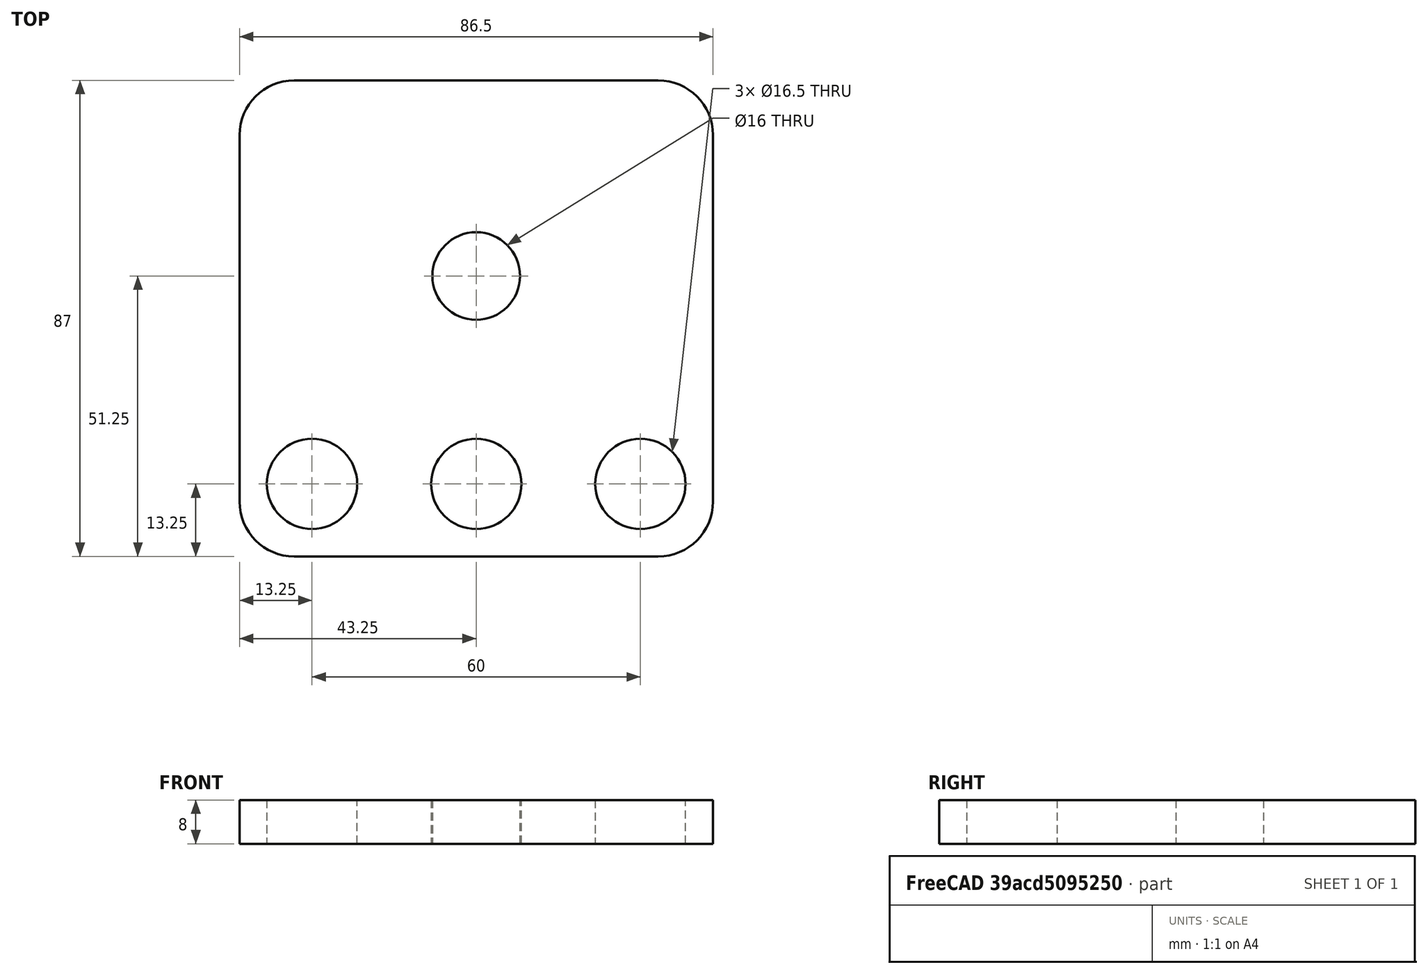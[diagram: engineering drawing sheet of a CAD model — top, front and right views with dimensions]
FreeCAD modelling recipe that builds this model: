
FCSTD DOCUMENT  (FreeCAD 0.19R24267 +99 (Git))
Label: V2 Allignment plate tabbed end plate
License: All rights reserved
LicenseURL: http://en.wikipedia.org/wiki/All_rights_reserved
objects: Sketcher::SketchObject×1, PartDesign::Pad×1, PartDesign::Body×1
note: 4 computed .brp shape members not serialized (recipe doc carries the construction recipe); baked Part::Feature solids carry a one-line shape summary decoded from their .brp

FEATURE [Sketcher::SketchObject] Sketch
  FullyConstrained = true
  MapMode = 5
  Support = -> [XY_Plane]
  sketch-geometry (17):
    g0: Circle CenterX=0 CenterY=0 CenterZ=0 NormalX=0 NormalY=0 NormalZ=1 AngleXU=0 Radius=6
    g1: Circle CenterX=0 CenterY=0 CenterZ=0 NormalX=0 NormalY=0 NormalZ=1 AngleXU=0 Radius=8
    g2: Circle CenterX=0 CenterY=-38 CenterZ=0 NormalX=0 NormalY=0 NormalZ=1 AngleXU=0 Radius=8.25
    g3: Circle CenterX=-30 CenterY=-38 CenterZ=0 NormalX=0 NormalY=0 NormalZ=1 AngleXU=0 Radius=8.25
    g4: Circle CenterX=30 CenterY=-38 CenterZ=0 NormalX=0 NormalY=0 NormalZ=1 AngleXU=0 Radius=8.25
    g5: LineSegment StartX=-30 StartY=-38 StartZ=0 EndX=30 EndY=-38 EndZ=0
    g6: LineSegment StartX=-33.25 StartY=-51.25 StartZ=0 EndX=33.25 EndY=-51.25 EndZ=0
    g7: LineSegment StartX=-43.25 StartY=-41.25 StartZ=0 EndX=-43.25 EndY=25.75 EndZ=0
    g8: LineSegment StartX=-33.25 StartY=35.75 StartZ=0 EndX=33.25 EndY=35.75 EndZ=0
    g9: LineSegment StartX=43.25 StartY=25.75 StartZ=0 EndX=43.25 EndY=-41.25 EndZ=0
    g10: ArcOfCircle CenterX=-33.25 CenterY=-41.25 CenterZ=0 NormalX=0 NormalY=0 NormalZ=1 AngleXU=0 Radius=10 StartAngle=3.14159 EndAngle=4.71239
    g11: ArcOfCircle CenterX=33.25 CenterY=-41.25 CenterZ=0 NormalX=0 NormalY=0 NormalZ=1 AngleXU=0 Radius=10 StartAngle=4.71239 EndAngle=6.28319
    g12: ArcOfCircle CenterX=33.25 CenterY=25.75 CenterZ=0 NormalX=0 NormalY=0 NormalZ=1 AngleXU=0 Radius=10 StartAngle=0 EndAngle=1.5708
    g13: ArcOfCircle CenterX=-33.25 CenterY=25.75 CenterZ=0 NormalX=0 NormalY=0 NormalZ=1 AngleXU=0 Radius=10 StartAngle=1.5708 EndAngle=3.14159
    g14: GeomPoint X=0 Y=-51.25 Z=0
    g15: LineSegment StartX=30 StartY=-38 StartZ=0 EndX=30 EndY=-51.25 EndZ=0
    g16: LineSegment StartX=30 StartY=-38 StartZ=0 EndX=43.25 EndY=-38 EndZ=0
  constraints (41):
    c: Coincident(g0,g-1)
    c: Diameter(g0) = 12
    c: Coincident(g1,g-1)
    c: Diameter(g1) = 16
    c: PointOnObject(g2,g-2)
    c: Symmetric(g3,g4,g-2)
    c: Coincident(g5,g3)
    c: Coincident(g5,g4)
    c: PointOnObject(g2,g5)
    c: Equal(g3,g2)
    c: Equal(g2,g4)
    c: Diameter(g4) = 16.5
    c: DistanceX(g5,g5) = 60
    c: DistanceY(g2,g1) = 38
    c: Vertical(g7)
    c: Horizontal(g8)
    c: Vertical(g9)
    c: Tangent(g6,g10) = -1.5708
    c: Tangent(g7,g10) = 1.5708
    c: Tangent(g6,g11) = -1.5708
    c: Tangent(g9,g11) = 1.5708
    c: Tangent(g8,g12) = 1.5708
    c: Tangent(g9,g12) = 1.5708
    c: Tangent(g8,g13) = 1.5708
    c: Tangent(g7,g13) = 1.5708
    c: Equal(g13,g12)
    c: Equal(g12,g11)
    c: Equal(g11,g10)
    c: Symmetric(g7,g9,g-2)
    c: DistanceY(g1,g8) = 35.75
    c: Radius(g13) = 10
    c: PointOnObject(g14,g6)
    c: PointOnObject(g14,g-2)
    c: Coincident(g15,g4)
    c: PointOnObject(g15,g6)
    c: Vertical(g15)
    c: Coincident(g16,g4)
    c: PointOnObject(g16,g9)
    c: Horizontal(g16)
    c: Equal(g15,g16)
    c: DistanceX(g16,g16) = 13.25
FEATURE [PartDesign::Pad] Pad  label="Thickness"
  Direction = (1,1,1)
  Length = 8
  Length2 = 100
  Profile = -> Sketch
  Type = 0
FEATURE [PartDesign::Body] Body
  Group = -> [Sketch,Pad]
  Origin = -> Origin
  Tip = -> Pad
